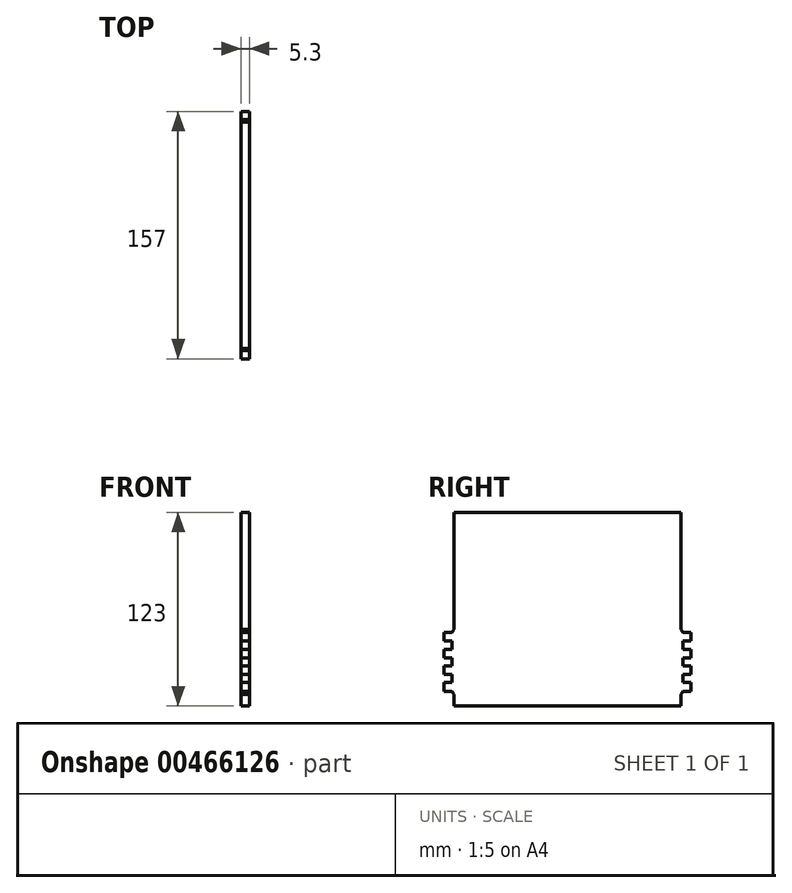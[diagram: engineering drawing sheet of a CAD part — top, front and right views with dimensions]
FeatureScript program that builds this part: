
annotation { "Feature Type Name" : "Feature", "Feature Type Description" : "" }
export const myFeature = defineFeature(function(context is Context, id is Id, definition is map)
    precondition{}
    {
        {
            var Q0;
            Q0=qCreatedBy(makeId("Right.planeOp"),FACE);
            var sketch = newSketch(context, id + "F0", { "sketchPlane" : qUnion([Q0])});
            skLineSegment(sketch, "E0.bottom", {"start": v(-73.3, 18.65) * mm, "end": v(-78.5, 18.65) * mm});
            skLineSegment(sketch, "E0.top", {"start": v(-73.3, 13.15) * mm, "end": v(-78.5, 13.15) * mm});
            skLineSegment(sketch, "E0.right", {"start": v(-78.5, 18.65) * mm, "end": v(-78.5, 13.15) * mm});
            skLineSegment(sketch, "E1.bottom", {"start": v(-73.3, 8.05) * mm, "end": v(-78.5, 8.05) * mm});
            skLineSegment(sketch, "E1.top", {"start": v(-73.3, 2.55) * mm, "end": v(-78.5, 2.55) * mm});
            skLineSegment(sketch, "E1.right", {"start": v(-78.5, 8.05) * mm, "end": v(-78.5, 2.55) * mm});
            skLineSegment(sketch, "E2", {"start": v(-73.3, 13.15) * mm, "end": v(-73.3, 8.05) * mm});
            skLineSegment(sketch, "E3.MirrorCS", {"start": v(-73.3, -18.65) * mm, "end": v(-78.5, -18.65) * mm});
            skLineSegment(sketch, "E4.MirrorCS", {"start": v(-73.3, -13.15) * mm, "end": v(-73.3, -8.05) * mm});
            skLineSegment(sketch, "E5.MirrorCS", {"start": v(-73.3, -13.15) * mm, "end": v(-78.5, -13.15) * mm});
            skLineSegment(sketch, "E6.MirrorCS", {"start": v(-73.3, -8.05) * mm, "end": v(-78.5, -8.05) * mm});
            skLineSegment(sketch, "E7.MirrorCS", {"start": v(-78.5, -18.65) * mm, "end": v(-78.5, -13.15) * mm});
            skLineSegment(sketch, "E8.MirrorCS", {"start": v(-78.5, -8.05) * mm, "end": v(-78.5, -2.55) * mm});
            skLineSegment(sketch, "E9.MirrorCS", {"start": v(-73.3, -2.55) * mm, "end": v(-78.5, -2.55) * mm});
            skLineSegment(sketch, "E10.MirrorCS", {"start": v(73.3, 18.65) * mm, "end": v(78.5, 18.65) * mm});
            skLineSegment(sketch, "E11.MirrorCS", {"start": v(73.3, -2.55) * mm, "end": v(78.5, -2.55) * mm});
            skLineSegment(sketch, "E12.MirrorCS", {"start": v(78.5, -8.05) * mm, "end": v(78.5, -2.55) * mm});
            skLineSegment(sketch, "E13.MirrorCS", {"start": v(78.5, -18.65) * mm, "end": v(78.5, -13.15) * mm});
            skLineSegment(sketch, "E14.MirrorCS", {"start": v(73.3, -8.05) * mm, "end": v(78.5, -8.05) * mm});
            skLineSegment(sketch, "E15.MirrorCS", {"start": v(73.3, -13.15) * mm, "end": v(78.5, -13.15) * mm});
            skLineSegment(sketch, "E16.MirrorCS", {"start": v(73.3, -13.15) * mm, "end": v(73.3, -8.05) * mm});
            skLineSegment(sketch, "E17.MirrorCS", {"start": v(73.3, -18.65) * mm, "end": v(78.5, -18.65) * mm});
            skLineSegment(sketch, "E18.MirrorCS", {"start": v(78.5, 18.65) * mm, "end": v(78.5, 13.15) * mm});
            skLineSegment(sketch, "E19.MirrorCS", {"start": v(73.3, 8.05) * mm, "end": v(78.5, 8.05) * mm});
            skLineSegment(sketch, "E20.MirrorCS", {"start": v(78.5, 8.05) * mm, "end": v(78.5, 2.55) * mm});
            skLineSegment(sketch, "E21.MirrorCS", {"start": v(73.3, 13.15) * mm, "end": v(73.3, 8.05) * mm});
            skLineSegment(sketch, "E22.MirrorCS", {"start": v(73.3, 2.55) * mm, "end": v(78.5, 2.55) * mm});
            skLineSegment(sketch, "E23.MirrorCS", {"start": v(73.3, 13.15) * mm, "end": v(78.5, 13.15) * mm});
            skLineSegment(sketch, "E24", {"start": v(-72, 95) * mm, "end": v(72, 95) * mm});
            skLineSegment(sketch, "E25", {"start": v(-73.3, 18.65) * mm, "end": v(-72, 20.65) * mm});
            skLineSegment(sketch, "E26", {"start": v(-72, 20.65) * mm, "end": v(-72, 95) * mm});
            skLineSegment(sketch, "E27", {"start": v(73.3, 18.65) * mm, "end": v(72, 20.65) * mm});
            skLineSegment(sketch, "E28", {"start": v(72, 20.65) * mm, "end": v(72, 95) * mm});
            skLineSegment(sketch, "E29", {"start": v(-73.3, 2.55) * mm, "end": v(-73.3, -2.55) * mm});
            skLineSegment(sketch, "E30", {"start": v(73.3, 2.55) * mm, "end": v(73.3, -2.55) * mm});
            skLineSegment(sketch, "E31.MirrorCS", {"start": v(-73.3, -18.65) * mm, "end": v(-72, -20.65) * mm});
            skLineSegment(sketch, "E32.MirrorCS", {"start": v(73.3, -18.65) * mm, "end": v(72, -20.65) * mm});
            skLineSegment(sketch, "E33", {"start": v(72, -20.65) * mm, "end": v(72, -28) * mm});
            skLineSegment(sketch, "E34", {"start": v(72, -28) * mm, "end": v(-72, -28) * mm});
            skLineSegment(sketch, "E35", {"start": v(-72, -28) * mm, "end": v(-72, -20.65) * mm});
            skSolve(sketch);
        }
        {
            var Q0;
            Q0 = qSketchRegion(id + "F0", true);
            extrude(context, id + "F1", {"entities" : qUnion([Q0]), "offsetDistance" : 25 * mm, "depth" : 5.3 * mm});
        }
    });
